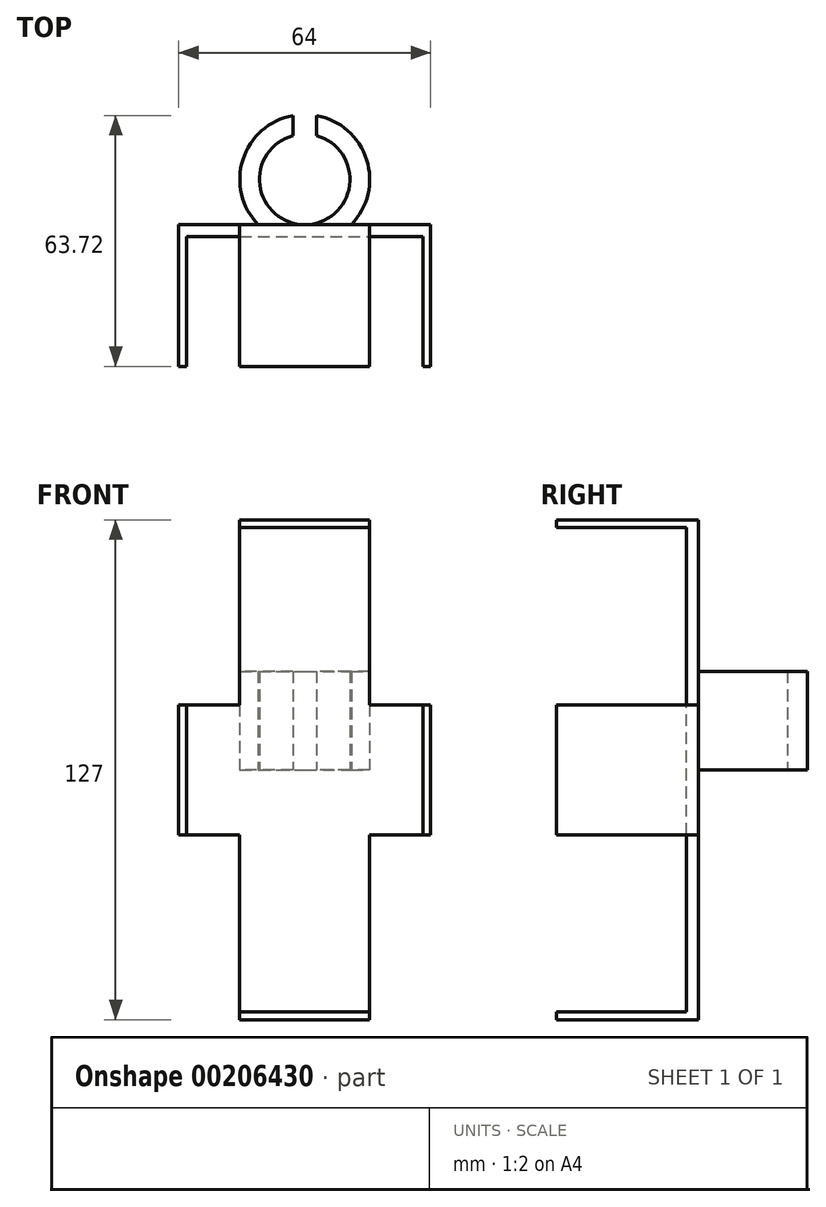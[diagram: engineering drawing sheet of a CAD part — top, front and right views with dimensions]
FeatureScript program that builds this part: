
annotation { "Feature Type Name" : "Feature", "Feature Type Description" : "" }
export const myFeature = defineFeature(function(context is Context, id is Id, definition is map)
    precondition{}
    {
        {
            var Q0;
            Q0=qCreatedBy(makeId("Front.planeOp"),FACE);
            var sketch = newSketch(context, id + "F0", { "sketchPlane" : qUnion([Q0])});
            skLineSegment(sketch, "E0.bottom", {"start": v(16.5, 63.5) * mm, "end": v(-16.5, 63.5) * mm});
            skLineSegment(sketch, "E0.top", {"start": v(16.5, -63.5) * mm, "end": v(-16.5, -63.5) * mm});
            skLineSegment(sketch, "E0.left", {"start": v(16.5, 63.5) * mm, "end": v(16.5, -63.5) * mm});
            skLineSegment(sketch, "E0.right", {"start": v(-16.5, 63.5) * mm, "end": v(-16.5, -63.5) * mm});
            skPoint(sketch, "E0.middle", {"position": v(0, 0) * mm});
            skLineSegment(sketch, "E1.bottom", {"start": v(32, 16.5) * mm, "end": v(-32, 16.5) * mm});
            skLineSegment(sketch, "E1.top", {"start": v(32, -16.5) * mm, "end": v(-32, -16.5) * mm});
            skLineSegment(sketch, "E1.left", {"start": v(32, 16.5) * mm, "end": v(32, -16.5) * mm});
            skLineSegment(sketch, "E1.right", {"start": v(-32, 16.5) * mm, "end": v(-32, -16.5) * mm});
            skSolve(sketch);
        }
        {
            var Q0;
            Q0 = qSketchRegion(id + "F0", true);
            extrude(context, id + "F1", {"entities" : qUnion([Q0]), "oppositeDirection" : true, "depth" : 3 * mm, "offsetDistance" : 25 * mm});
        }
        {
            var Q0;
            Q0=makeQuery(id+"F1.opExtrude","CAP_FACE",FACE,{"disambiguationData":[OSD([sQuery(id+"F0.wireOp",EDGE,"E0.bottom"),sQuery(id+"F0.wireOp",EDGE,"E0.top"),sQuery(id+"F0.wireOp",EDGE,"E0.left"),sQuery(id+"F0.wireOp",EDGE,"E0.right"),sQuery(id+"F0.wireOp",EDGE,"E1.bottom"),sQuery(id+"F0.wireOp",EDGE,"E1.top"),sQuery(id+"F0.wireOp",EDGE,"E1.left"),sQuery(id+"F0.wireOp",EDGE,"E1.right")])],"isStart":true});
            var sketch = newSketch(context, id + "F2", { "sketchPlane" : qUnion([Q0])});
            skLineSegment(sketch, "E2", {"start": v(-16.5, 61.5) * mm, "end": v(16.5, 61.5) * mm});
            skLineSegment(sketch, "E3", {"start": v(-30, 16.5) * mm, "end": v(-30, -16.5) * mm});
            skPoint(sketch, "E3.endSnap0", {"position": v(-24.25, -16.5) * mm});
            skLineSegment(sketch, "E4", {"start": v(-16.5, -61.5) * mm, "end": v(16.5, -61.5) * mm});
            skLineSegment(sketch, "E5", {"start": v(30, -16.5) * mm, "end": v(30, 16.5) * mm});
            skSolve(sketch);
        }
        {
            var Q0;
            {var subQ0=sQuery(id+"F2.wireOp",EDGE,"E2");Q0=makeQuery(id+"F2.imprint","IMPRINT",FACE,{"disambiguationData":[TD([[makeQuery(id+"F2.imprint","IMPRINT",EDGE,{"derivedFrom":subQ0}),1.0]])]});}
            var Q1;
            {var subQ0=sQuery(id+"F2.wireOp",EDGE,"E3");Q1=makeQuery(id+"F2.imprint","IMPRINT",FACE,{"disambiguationData":[TD([[makeQuery(id+"F2.imprint","IMPRINT",EDGE,{"derivedFrom":subQ0}),-1.0]])]});}
            var Q2;
            {var subQ0=sQuery(id+"F2.wireOp",EDGE,"E4");Q2=makeQuery(id+"F2.imprint","IMPRINT",FACE,{"disambiguationData":[TD([[makeQuery(id+"F2.imprint","IMPRINT",EDGE,{"derivedFrom":subQ0}),-1.0]])]});}
            var Q3;
            {var subQ0=sQuery(id+"F2.wireOp",EDGE,"E5");Q3=makeQuery(id+"F2.imprint","IMPRINT",FACE,{"disambiguationData":[TD([[makeQuery(id+"F2.imprint","IMPRINT",EDGE,{"derivedFrom":subQ0}),-1.0]])]});}
            extrude(context, id + "F3", {"entities" : qUnion([Q0, Q1, Q2, Q3]), "operationType" : NewBodyOperationType.ADD, "depth" : 33 * mm, "offsetDistance" : 25 * mm});
        }
        {
            var Q0;
            Q0=qCreatedBy(makeId("Top.planeOp"),FACE);
            var sketch = newSketch(context, id + "F4", { "sketchPlane" : qUnion([Q0])});
            skCircle(sketch, "E6", {"center": v(0, 14.5) * mm, "radius": 11.5 * mm});
            skCircle(sketch, "E7.0", {"center": v(0, 14.5) * mm, "radius": 16.5 * mm});
            skLineSegment(sketch, "E8", {"start": v(-3, 30.72) * mm, "end": v(-3, 25.6) * mm});
            skLineSegment(sketch, "E9", {"start": v(3, 30.72) * mm, "end": v(3, 25.6) * mm});
            skLineSegment(sketch, "E10", {"start": v(-11.83, 3) * mm, "end": v(11.83, 3) * mm});
            skSolve(sketch);
        }
        {
            var Q0;
            {var subQ0=sQuery(id+"F4.wireOp",EDGE,"E8");Q0=makeQuery(id+"F4.imprint","IMPRINT",FACE,{"disambiguationData":[TD([[makeQuery(id+"F4.imprint","IMPRINT",EDGE,{"derivedFrom":subQ0}),-1.0]])]});}
            var Q1;
            {var subQ0=sQuery(id+"F4.wireOp",EDGE,"E9");Q1=makeQuery(id+"F4.imprint","IMPRINT",FACE,{"disambiguationData":[TD([[makeQuery(id+"F4.imprint","IMPRINT",EDGE,{"derivedFrom":subQ0}),1.0]])]});}
            extrude(context, id + "F5", {"entities" : qUnion([Q0, Q1]), "operationType" : NewBodyOperationType.ADD, "depth" : 25 * mm, "offsetDistance" : 25 * mm});
        }
    });
